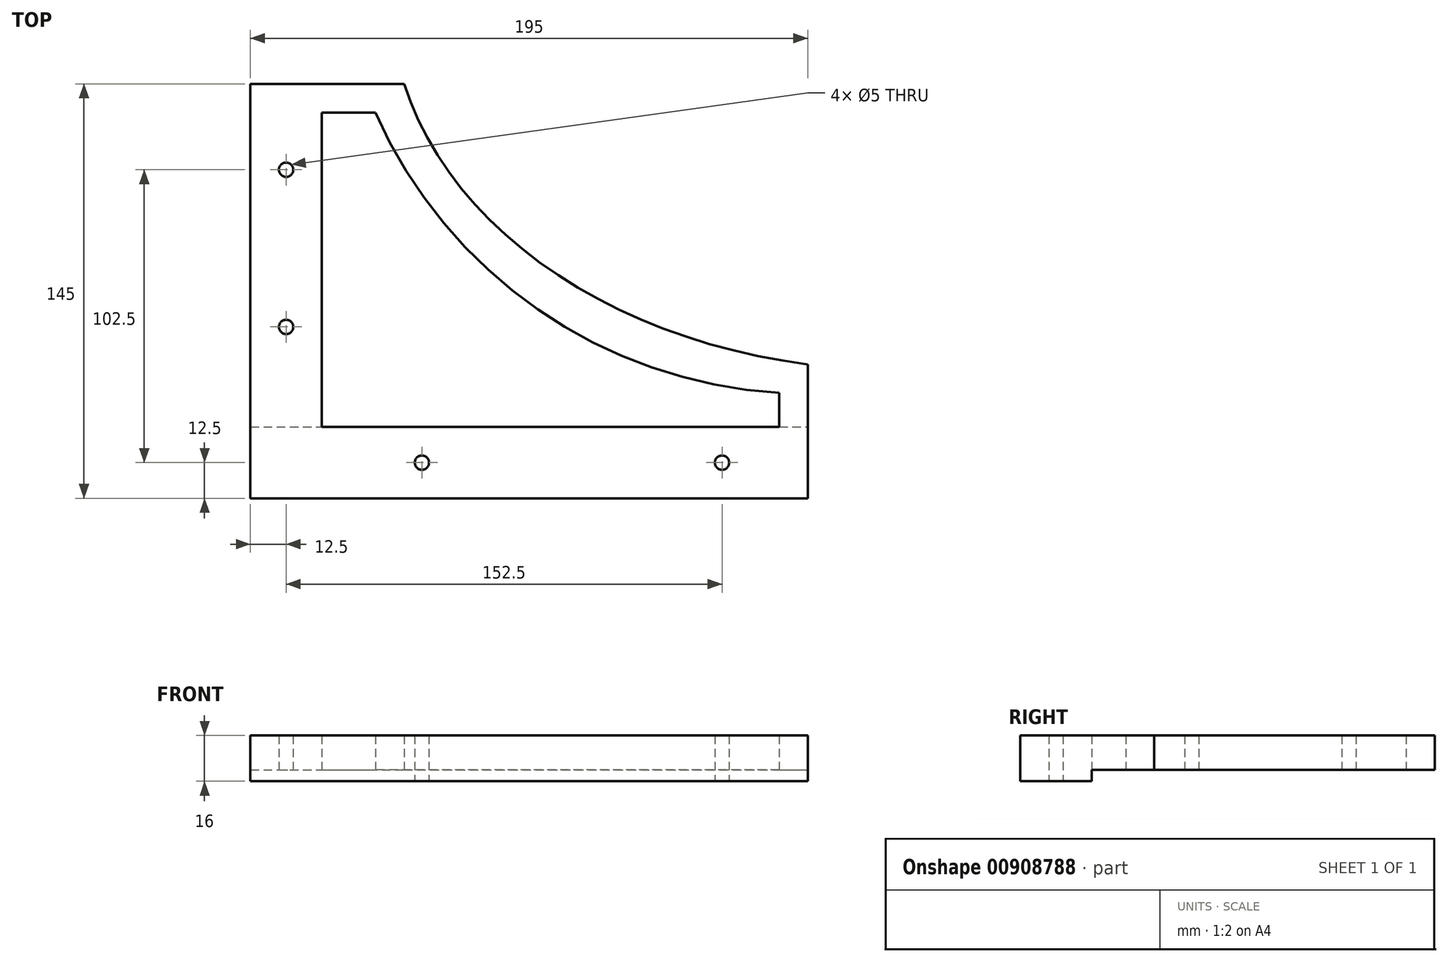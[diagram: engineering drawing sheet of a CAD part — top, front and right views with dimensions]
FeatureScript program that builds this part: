
annotation { "Feature Type Name" : "Feature", "Feature Type Description" : "" }
export const myFeature = defineFeature(function(context is Context, id is Id, definition is map)
    precondition{}
    {
        {
            var Q0;
            Q0=qCreatedBy(makeId("Top.planeOp"),FACE);
            var sketch = newSketch(context, id + "F0", { "sketchPlane" : qUnion([Q0])});
            skEllipticalArc(sketch, "E0", {});
            skLineSegment(sketch, "E1", {"start": v(-176, 0) * mm, "end": v(-176, -130) * mm});
            skPoint(sketch, "E1.endSnap0", {"position": v(0, -130) * mm});
            skLineSegment(sketch, "E2", {"start": v(-176, -130) * mm, "end": v(0, -130) * mm});
            skLineSegment(sketch, "E3", {"start": v(-176, 0) * mm, "end": v(-200, 0) * mm});
            skLineSegment(sketch, "E4", {"start": v(-200, 0) * mm, "end": v(-200, -150) * mm});
            skLineSegment(sketch, "E5", {"start": v(-200, -150) * mm, "end": v(0, -150) * mm});
            skLineSegment(sketch, "E6", {"start": v(0, -150) * mm, "end": v(0, -130) * mm});
            const initialGuessF0  = {"E0": [0, 0, 1, 0, 0.176, 0.13, 3.141592653589793, 4.71238898038469]};
            skSetInitialGuess(sketch, initialGuessF0);
            skSolve(sketch);
        }
        {
            var Q0;
            Q0=qSketchRegion(id+"F0",true);
            extrude(context, id + "F1", {"entities" : qUnion([Q0]), "depth" : 12 * mm, "offsetDistance" : 25 * mm});
        }
        {
            var Q0;
            Q0=makeQuery(id+"F1.opExtrude","SWEPT_FACE",FACE,{"disambiguationData":[OSD([sQuery(id+"F0.wireOp",EDGE,"E5")])]});
            var sketch = newSketch(context, id + "F2", { "sketchPlane" : qUnion([Q0])});
            skLineSegment(sketch, "E7.bottom", {"start": v(-200, 16) * mm, "end": v(0, 16) * mm});
            skLineSegment(sketch, "E7.top", {"start": v(-200, -4) * mm, "end": v(0, -4) * mm});
            skLineSegment(sketch, "E7.left", {"start": v(-200, 16) * mm, "end": v(-200, -4) * mm});
            skLineSegment(sketch, "E7.right", {"start": v(0, 16) * mm, "end": v(0, -4) * mm});
            skSolve(sketch);
        }
        {
            var Q0;
            Q0=qSketchRegion(id+"F2",true);
            extrude(context, id + "F3", {"entities" : qUnion([Q0]), "operationType" : NewBodyOperationType.ADD, "depth" : 5 * mm, "offsetDistance" : 25 * mm});
        }
        {
            var Q0;
            Q0=makeQuery(id+"F3.boolean.opBoolean","MERGE",FACE,{"derivedFrom":[makeQuery(id+"F1.opExtrude","SWEPT_FACE",FACE,{"disambiguationData":[OSD([sQuery(id+"F0.wireOp",EDGE,"E4")])]}),makeQuery(id+"F3.opExtrude","SWEPT_FACE",FACE,{"disambiguationData":[OSD([sQuery(id+"F2.wireOp",EDGE,"E7.left")])]})]});
            var sketch = newSketch(context, id + "F4", { "sketchPlane" : qUnion([Q0])});
            skLineSegment(sketch, "E8.bottom", {"start": v(155, 16) * mm, "end": v(0, 16) * mm});
            skLineSegment(sketch, "E8.top", {"start": v(155, -4) * mm, "end": v(0, -4) * mm});
            skLineSegment(sketch, "E8.left", {"start": v(155, 16) * mm, "end": v(155, -4) * mm});
            skLineSegment(sketch, "E8.right", {"start": v(0, 16) * mm, "end": v(0, -4) * mm});
            skSolve(sketch);
        }
        {
            var Q0;
            Q0=qSketchRegion(id+"F4",true);
            extrude(context, id + "F5", {"entities" : qUnion([Q0]), "operationType" : NewBodyOperationType.ADD, "depth" : 5 * mm, "offsetDistance" : 25 * mm});
        }
        {
            var Q0;
            Q0=makeQuery(id+"F5.boolean.opBoolean","MERGE",FACE,{"derivedFrom":[makeQuery(id+"F3.opExtrude","SWEPT_FACE",FACE,{"disambiguationData":[OSD([sQuery(id+"F2.wireOp",EDGE,"E7.top")])]}),makeQuery(id+"F5.opExtrude","SWEPT_FACE",FACE,{"disambiguationData":[OSD([sQuery(id+"F4.wireOp",EDGE,"E8.top")])]})]});
            var sketch = newSketch(context, id + "F6", { "sketchPlane" : qUnion([Q0])});
            skLineSegment(sketch, "E9", {"start": v(0, 175) * mm, "end": v(-225, 175) * mm});
            skLineSegment(sketch, "E10", {"start": v(-225, 175) * mm, "end": v(-225, 0) * mm});
            skLineSegment(sketch, "E11", {"start": v(-225, 0) * mm, "end": v(-205, 0) * mm});
            skLineSegment(sketch, "E12", {"start": v(-205, 0) * mm, "end": v(-205, 155) * mm});
            skLineSegment(sketch, "E13", {"start": v(-205, 155) * mm, "end": v(0, 155) * mm});
            skLineSegment(sketch, "E14", {"start": v(0, 155) * mm, "end": v(0, 175) * mm});
            skCircle(sketch, "E15", {"center": v(-212.5, 60) * mm, "radius": 2.5 * mm});
            skCircle(sketch, "E16", {"center": v(-212.5, 115) * mm, "radius": 2.5 * mm});
            skCircle(sketch, "E17", {"center": v(-165, 162.5) * mm, "radius": 2.5 * mm});
            skCircle(sketch, "E18", {"center": v(-60, 162.5) * mm, "radius": 2.5 * mm});
            skSolve(sketch);
        }
        {
            var Q0;
            Q0=qSketchRegion(id+"F6",true);
            extrude(context, id + "F7", {"entities" : qUnion([Q0]), "operationType" : NewBodyOperationType.ADD, "oppositeDirection" : true, "depth" : 25 * mm, "offsetDistance" : 25 * mm});
        }
        {
            var Q0;
            Q0=makeQuery(id+"F5.boolean.opBoolean","MERGE",FACE,{"derivedFrom":[makeQuery(id+"F3.opExtrude","SWEPT_FACE",FACE,{"disambiguationData":[OSD([sQuery(id+"F2.wireOp",EDGE,"E7.bottom")])]}),makeQuery(id+"F5.opExtrude","SWEPT_FACE",FACE,{"disambiguationData":[OSD([sQuery(id+"F4.wireOp",EDGE,"E8.bottom")])]})]});
            var sketch = newSketch(context, id + "F8", { "sketchPlane" : qUnion([Q0])});
            skLineSegment(sketch, "E19", {"start": v(-205, 0) * mm, "end": v(-190, 0) * mm});
            skLineSegment(sketch, "E20", {"start": v(-190, 0) * mm, "end": v(-190, -140) * mm});
            skLineSegment(sketch, "E21", {"start": v(-190, -140) * mm, "end": v(0, -140) * mm});
            skLineSegment(sketch, "E22", {"start": v(0, -140) * mm, "end": v(0, -155) * mm});
            skLineSegment(sketch, "E23", {"start": v(0, -155) * mm, "end": v(-205, -155) * mm});
            skLineSegment(sketch, "E24", {"start": v(-205, -155) * mm, "end": v(-205, 0) * mm});
            skSolve(sketch);
        }
        {
            var Q0;
            Q0=qSketchRegion(id+"F8",true);
            extrude(context, id + "F9", {"entities" : qUnion([Q0]), "operationType" : NewBodyOperationType.ADD, "depth" : 5 * mm, "offsetDistance" : 25 * mm});
        }
        {
            var Q0;
            Q0=qCreatedBy(makeId("Top.planeOp"),FACE);
            var sketch = newSketch(context, id + "F10", { "sketchPlane" : qUnion([Q0])});
            skLineSegment(sketch, "E25.bottom", {"start": v(-225, 0) * mm, "end": v(0, 0) * mm});
            skLineSegment(sketch, "E25.top", {"start": v(-225, -30) * mm, "end": v(0, -30) * mm});
            skLineSegment(sketch, "E25.left", {"start": v(-225, 0) * mm, "end": v(-225, -30) * mm});
            skLineSegment(sketch, "E25.right", {"start": v(0, 0) * mm, "end": v(0, -30) * mm});
            skLineSegment(sketch, "E26.bottom", {"start": v(0, -175) * mm, "end": v(-30, -175) * mm});
            skLineSegment(sketch, "E26.top", {"start": v(0, 0) * mm, "end": v(-30, 0) * mm});
            skLineSegment(sketch, "E26.left", {"start": v(0, -175) * mm, "end": v(0, 0) * mm});
            skLineSegment(sketch, "E26.right", {"start": v(-30, -175) * mm, "end": v(-30, 0) * mm});
            skSolve(sketch);
        }
        {
            var Q0;
            Q0=qSketchRegion(id+"F10",true);
            extrude(context, id + "F11", {"entities" : qUnion([Q0]), "operationType" : NewBodyOperationType.REMOVE, "endBound" : BoundingType.SYMMETRIC, "oppositeDirection" : true, "depth" : 50 * mm, "offsetDistance" : 25 * mm});
        }
        {
            var Q0;
            Q0=makeQuery(id+"F11.boolean.opBoolean","COPY",FACE,{"derivedFrom":makeQuery(id+"F11.opExtrude","SWEPT_FACE",FACE,{"disambiguationData":[OSD([sQuery(id+"F10.wireOp",EDGE,"E26.right")])]})});
            var sketch = newSketch(context, id + "F12", { "sketchPlane" : qUnion([Q0])});
            skLineSegment(sketch, "E27.bottom", {"start": v(-175, 21) * mm, "end": v(-30, 21) * mm});
            skLineSegment(sketch, "E27.top", {"start": v(-175, 12) * mm, "end": v(-30, 12) * mm});
            skLineSegment(sketch, "E27.left", {"start": v(-175, 21) * mm, "end": v(-175, 12) * mm});
            skLineSegment(sketch, "E27.right", {"start": v(-30, 21) * mm, "end": v(-30, 12) * mm});
            skSolve(sketch);
        }
        {
            var Q0;
            Q0=qSketchRegion(id+"F12",true);
            extrude(context, id + "F13", {"entities" : qUnion([Q0]), "operationType" : NewBodyOperationType.REMOVE, "endBound" : BoundingType.THROUGH_ALL, "oppositeDirection" : true, "depth" : 25 * mm, "offsetDistance" : 25 * mm});
        }
        {
            var Q0;
            Q0=makeQuery(id+"F1.opExtrude","CAP_FACE",FACE,{"disambiguationData":[OSD([sQuery(id+"F0.wireOp",EDGE,"E0"),sQuery(id+"F0.wireOp",EDGE,"E3"),sQuery(id+"F0.wireOp",EDGE,"E4"),sQuery(id+"F0.wireOp",EDGE,"E5"),sQuery(id+"F0.wireOp",EDGE,"E6")])],"isStart":true});
            var sketch = newSketch(context, id + "F14", { "sketchPlane" : qUnion([Q0])});
            skLineSegment(sketch, "E28", {"start": v(-40, 138.1) * mm, "end": v(-40, 150) * mm});
            skLineSegment(sketch, "E29", {"start": v(-40, 150) * mm, "end": v(-200, 150) * mm});
            skLineSegment(sketch, "E30", {"start": v(-200, 150) * mm, "end": v(-200, 40) * mm});
            skLineSegment(sketch, "E31", {"start": v(-200, 40) * mm, "end": v(-181.25, 40) * mm});
            skArc(sketch, "E32", {"start": v(-40, 138.1) * mm, "mid": v(-124.42, 108.9) * mm, "end": v(-181.25, 40) * mm});
            skSolve(sketch);
        }
        {
            var Q0;
            Q0=qSketchRegion(id+"F14",true);
            extrude(context, id + "F15", {"entities" : qUnion([Q0]), "operationType" : NewBodyOperationType.REMOVE, "oppositeDirection" : true, "depth" : 25 * mm, "offsetDistance" : 25 * mm});
        }
        {
            var Q0;
            {var subQ0=sQuery(id+"F2.wireOp",EDGE,"E7.top");var subQ2=sQuery(id+"F4.wireOp",EDGE,"E8.top");var subQ3=sQuery(id+"F4.wireOp",EDGE,"E8.right");Q0=makeQuery(id+"F15.boolean.opBoolean","MERGE",FACE,{"derivedFrom":[makeQuery(id+"F5.boolean.opBoolean","SPLIT",FACE,{"disambiguationData":[TD([makeQuery(id+"F3.opExtrude","SWEPT_FACE",FACE,{"disambiguationData":[OSD([subQ0])]})])],"derivedFrom":makeQuery(id+"F5.opExtrude","CAP_FACE",FACE,{"disambiguationData":[OSD([sQuery(id+"F4.wireOp",EDGE,"E8.bottom"),subQ2,sQuery(id+"F4.wireOp",EDGE,"E8.left"),subQ3])],"isStart":true})})],"fromTools":[makeQuery(id+"F15.opExtrude","SWEPT_FACE",FACE,{"disambiguationData":[OSD([sQuery(id+"F14.wireOp",EDGE,"E30")])]})]});}
            var sketch = newSketch(context, id + "F16", { "sketchPlane" : qUnion([Q0])});
            skLineSegment(sketch, "E33.bottom", {"start": v(-150, -4) * mm, "end": v(-30, -4) * mm});
            skLineSegment(sketch, "E33.top", {"start": v(-150, 0) * mm, "end": v(-30, 0) * mm});
            skLineSegment(sketch, "E33.left", {"start": v(-150, -4) * mm, "end": v(-150, 0) * mm});
            skLineSegment(sketch, "E33.right", {"start": v(-30, -4) * mm, "end": v(-30, 0) * mm});
            skSolve(sketch);
        }
        {
            var Q0;
            Q0=makeQuery(id+"F16.imprint","IMPRINT",FACE,{"disambiguationData":[TD([[makeQuery(id+"F16.imprint","IMPRINT",EDGE,{"derivedFrom":sQuery(id+"F16.wireOp",EDGE,"E33.bottom")}),1.0]])]});
            extrude(context, id + "F17", {"entities" : qUnion([Q0]), "operationType" : NewBodyOperationType.REMOVE, "endBound" : BoundingType.UP_TO_NEXT, "oppositeDirection" : true, "depth" : 25 * mm, "offsetDistance" : 25 * mm});
        }
    });
